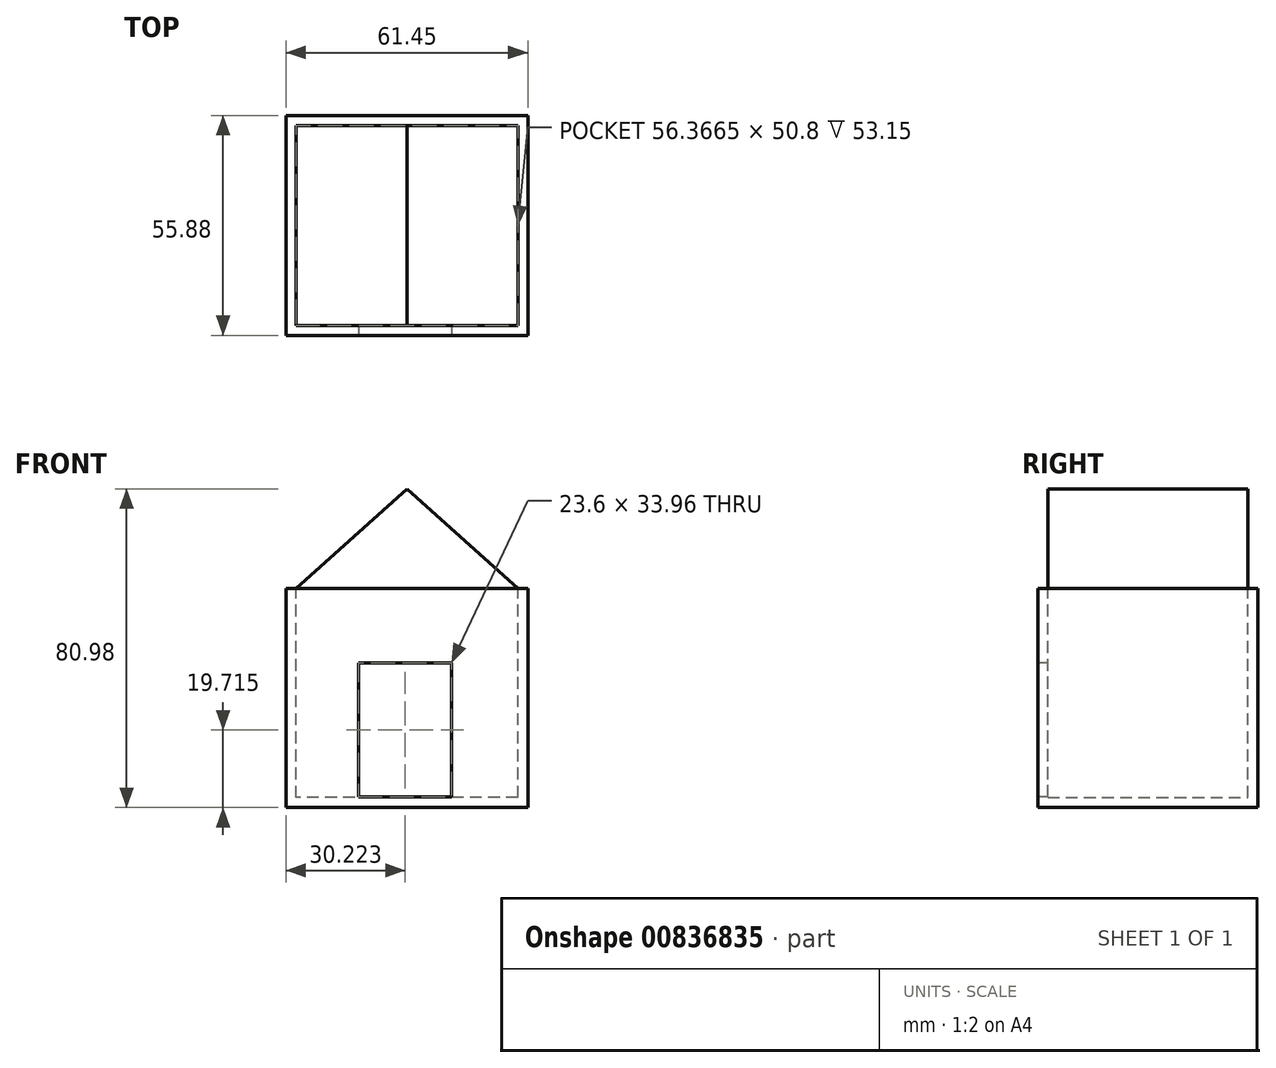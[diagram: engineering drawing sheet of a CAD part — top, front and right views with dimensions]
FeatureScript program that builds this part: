
annotation { "Feature Type Name" : "Feature", "Feature Type Description" : "" }
export const myFeature = defineFeature(function(context is Context, id is Id, definition is map)
    precondition{}
    {
        {
            var Q0;
            Q0=qCreatedBy(makeId("Front.planeOp"),FACE);
            var sketch = newSketch(context, id + "F0", { "sketchPlane" : qUnion([Q0])});
            skLineSegment(sketch, "E0.bottom", {"start": v(0, 0) * mm, "end": v(-61.45, 0) * mm});
            skLineSegment(sketch, "E0.top", {"start": v(0, 55.7) * mm, "end": v(-61.45, 55.7) * mm});
            skLineSegment(sketch, "E0.left", {"start": v(0, 0) * mm, "end": v(0, 55.7) * mm});
            skLineSegment(sketch, "E0.right", {"start": v(-61.45, 0) * mm, "end": v(-61.45, 55.7) * mm});
            skSolve(sketch);
        }
        {
            var Q0;
            Q0=makeQuery(id+"F0.imprint","IMPRINT",FACE,{"disambiguationData":[TD([[makeQuery(id+"F0.imprint","IMPRINT",EDGE,{"derivedFrom":sQuery(id+"F0.wireOp",EDGE,"E0.bottom")}),-1.0]])]});
            extrude(context, id + "F1", {"entities" : qUnion([Q0]), "depth" : 55.88 * mm, "offsetDistance" : 25.4 * mm});
        }
        {
            var Q0;
            Q0=makeQuery(id+"F1.opExtrude","SWEPT_FACE",FACE,{"disambiguationData":[OSD([sQuery(id+"F0.wireOp",EDGE,"E0.top")])]});
            shell(context, id + "F2", {"entities" : qUnion([Q0]), "thickness" : 2.54 * mm});
        }
        {
            var Q0;
            Q0=makeQuery(id+"F1.opExtrude","CAP_FACE",FACE,{"disambiguationData":[OSD([sQuery(id+"F0.wireOp",EDGE,"E0.bottom"),sQuery(id+"F0.wireOp",EDGE,"E0.top"),sQuery(id+"F0.wireOp",EDGE,"E0.left"),sQuery(id+"F0.wireOp",EDGE,"E0.right")])],"isStart":false});
            var sketch = newSketch(context, id + "F3", { "sketchPlane" : qUnion([Q0])});
            skLineSegment(sketch, "E1.bottom", {"start": v(-43.03, 2.73) * mm, "end": v(-19.43, 2.73) * mm});
            skLineSegment(sketch, "E1.top", {"start": v(-43.03, 36.7) * mm, "end": v(-19.43, 36.7) * mm});
            skLineSegment(sketch, "E1.left", {"start": v(-43.03, 2.73) * mm, "end": v(-43.03, 36.7) * mm});
            skLineSegment(sketch, "E1.right", {"start": v(-19.43, 2.73) * mm, "end": v(-19.43, 36.7) * mm});
            skSolve(sketch);
        }
        {
            var Q0;
            Q0=makeQuery(id+"F3.imprint","IMPRINT",FACE,{"disambiguationData":[TD([[makeQuery(id+"F3.imprint","IMPRINT",EDGE,{"derivedFrom":sQuery(id+"F3.wireOp",EDGE,"E1.bottom")}),1.0]])]});
            extrude(context, id + "F4", {"entities" : qUnion([Q0]), "operationType" : NewBodyOperationType.REMOVE, "oppositeDirection" : true, "depth" : 25.4 * mm, "offsetDistance" : 25.4 * mm});
        }
        {
            var Q0;
            {var subQ0=sQuery(id+"F0.wireOp",EDGE,"E0.right");var subQ1=sQuery(id+"F0.wireOp",EDGE,"E0.left");var subQ2=sQuery(id+"F0.wireOp",EDGE,"E0.top");var subQ3=sQuery(id+"F0.wireOp",EDGE,"E0.bottom");Q0=makeQuery(id+"F2.opShell","OFFSET_FACE",FACE,{"disambiguationData":[OSD([subQ3,subQ2,subQ1,subQ0]),TDD([makeQuery(id+"F1.opExtrude","CAP_FACE",FACE,{"disambiguationData":[OSD([subQ3,subQ2,subQ1,subQ0])],"isStart":true})])]});}
            var sketch = newSketch(context, id + "F5", { "sketchPlane" : qUnion([Q0])});
            skLineSegment(sketch, "E2", {"start": v(-58.9, 55.7) * mm, "end": v(-2.54, 55.7) * mm});
            skLineSegment(sketch, "E3", {"start": v(-2.54, 55.7) * mm, "end": v(-30.72, 80.98) * mm});
            skPoint(sketch, "E3.endSnap0", {"position": v(-30.72, 55.7) * mm});
            skLineSegment(sketch, "E4", {"start": v(-30.72, 80.98) * mm, "end": v(-58.9, 55.7) * mm});
            skSolve(sketch);
        }
        {
            var Q0;
            Q0=makeQuery(id+"F5.imprint","IMPRINT",FACE,{"disambiguationData":[TD([[makeQuery(id+"F5.imprint","IMPRINT",EDGE,{"derivedFrom":sQuery(id+"F5.wireOp",EDGE,"E2")}),-1.0]])]});
            extrude(context, id + "F6", {"entities" : qUnion([Q0]), "depth" : 50.8 * mm, "offsetDistance" : 25.4 * mm});
        }
    });
